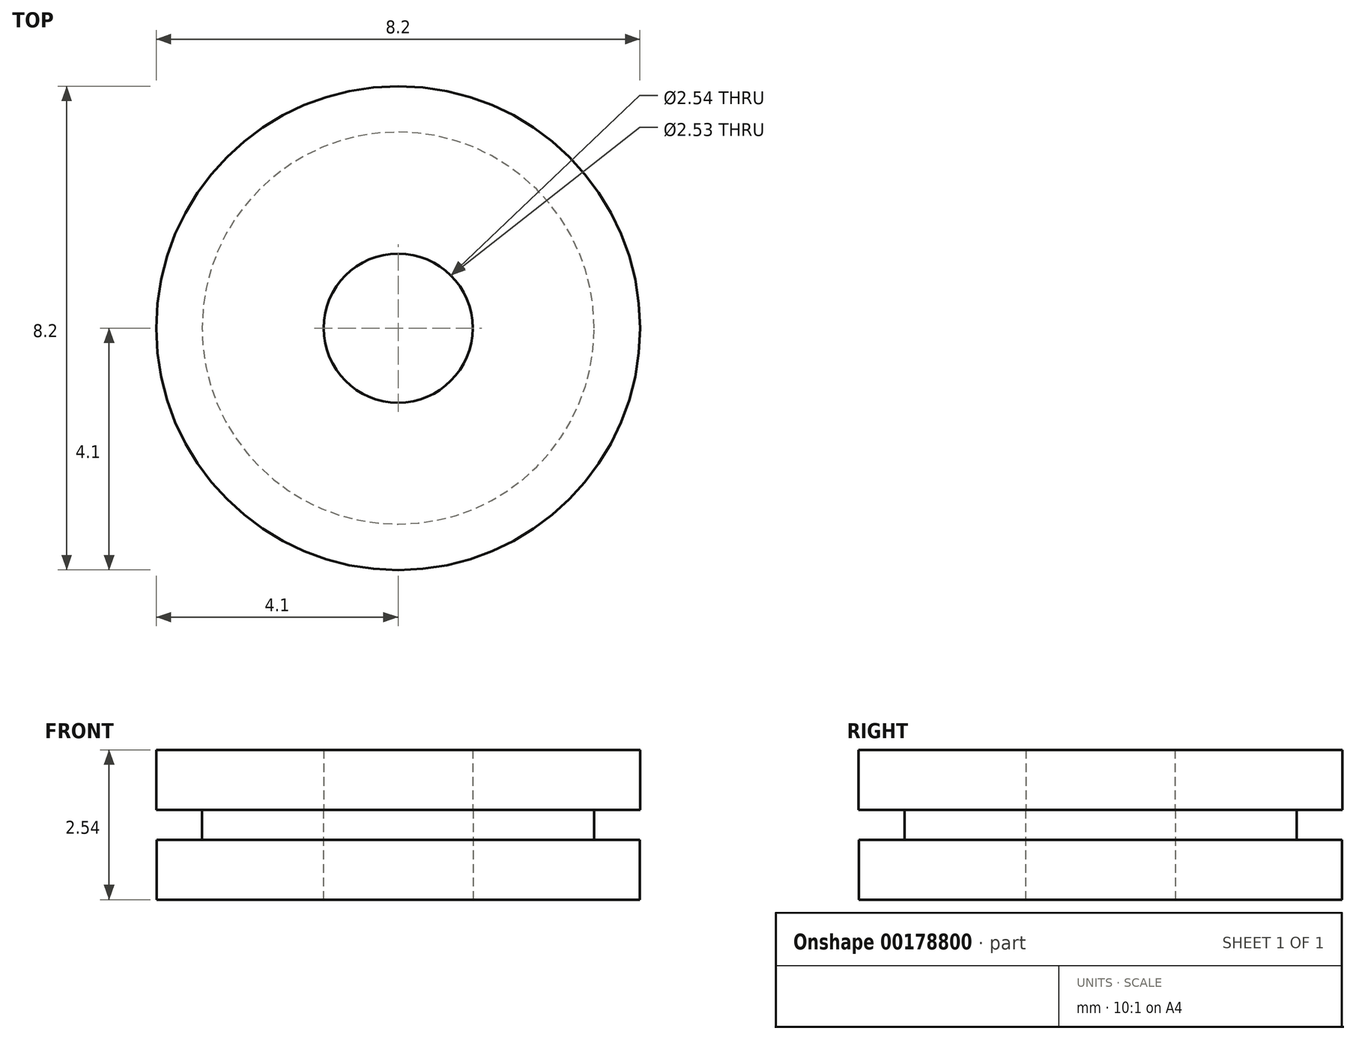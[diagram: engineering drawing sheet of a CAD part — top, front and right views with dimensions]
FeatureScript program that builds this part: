
annotation { "Feature Type Name" : "Feature", "Feature Type Description" : "" }
export const myFeature = defineFeature(function(context is Context, id is Id, definition is map)
    precondition{}
    {
        {
            var Q0;
            Q0=qCreatedBy(makeId("Top.planeOp"),FACE);
            var sketch = newSketch(context, id + "F0", { "sketchPlane" : qUnion([Q0])});
            skCircle(sketch, "E0", {"center": v(0, 0) * mm, "radius": 1.27 * mm});
            skCircle(sketch, "E1", {"center": v(0, 0) * mm, "radius": 4.1 * mm});
            skSolve(sketch);
        }
        {
            var Q0;
            Q0=makeQuery(id+"F0.imprint","IMPRINT",FACE,{"disambiguationData":[TD([[makeQuery(id+"F0.imprint","IMPRINT",EDGE,{"derivedFrom":sQuery(id+"F0.wireOp",EDGE,"E0")}),-1.0]])]});
            extrude(context, id + "F1", {"entities" : qUnion([Q0]), "depth" : 1.02 * mm});
        }
        {
            var Q0;
            Q0=makeQuery(id+"F1.opExtrude","CAP_FACE",FACE,{"disambiguationData":[OSD([sQuery(id+"F0.wireOp",EDGE,"E0"),sQuery(id+"F0.wireOp",EDGE,"E1")])],"isStart":false});
            var sketch = newSketch(context, id + "F2", { "sketchPlane" : qUnion([Q0])});
            skCircle(sketch, "E2", {"center": v(0, 0) * mm, "radius": 3.32 * mm});
            skCircle(sketch, "E3", {"center": v(0, 0) * mm, "radius": 1.27 * mm});
            skSolve(sketch);
        }
        {
            var Q0;
            Q0=makeQuery(id+"F2.imprint","IMPRINT",FACE,{"disambiguationData":[TD([[makeQuery(id+"F2.imprint","IMPRINT",EDGE,{"derivedFrom":sQuery(id+"F2.wireOp",EDGE,"E2")}),1.0]])]});
            extrude(context, id + "F3", {"entities" : qUnion([Q0]), "operationType" : NewBodyOperationType.ADD, "depth" : 0.5 * mm});
        }
        {
            var Q0;
            Q0=makeQuery(id+"F3.opExtrude","CAP_FACE",FACE,{"disambiguationData":[OSD([sQuery(id+"F2.wireOp",EDGE,"E2"),sQuery(id+"F2.wireOp",EDGE,"E3")])],"isStart":false});
            var sketch = newSketch(context, id + "F4", { "sketchPlane" : qUnion([Q0])});
            skCircle(sketch, "E4", {"center": v(0, 0) * mm, "radius": 1.26 * mm});
            skCircle(sketch, "E5", {"center": v(0, 0) * mm, "radius": 4.1 * mm});
            skSolve(sketch);
        }
        {
            var Q0;
            Q0 = qSketchRegion(id + "F4", true);
            extrude(context, id + "F5", {"entities" : qUnion([Q0]), "operationType" : NewBodyOperationType.ADD, "depth" : 1.02 * mm});
        }
    });
